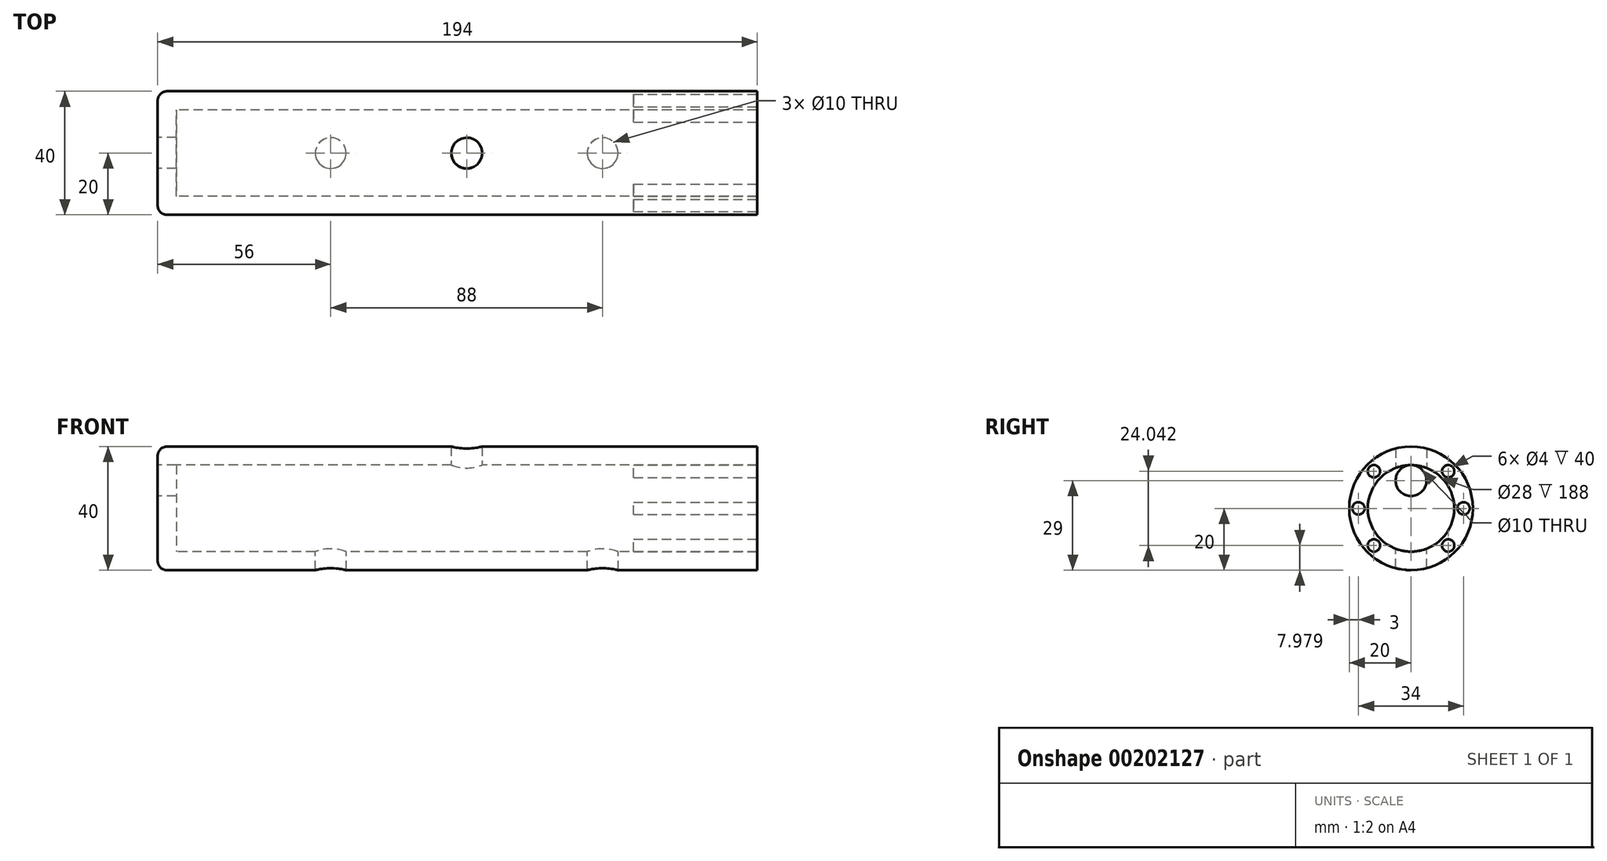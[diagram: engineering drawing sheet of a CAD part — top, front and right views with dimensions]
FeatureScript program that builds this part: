
annotation { "Feature Type Name" : "Feature", "Feature Type Description" : "" }
export const myFeature = defineFeature(function(context is Context, id is Id, definition is map)
    precondition{}
    {
        {
            var Q0;
            Q0=qCreatedBy(makeId("Right.planeOp"),FACE);
            var sketch = newSketch(context, id + "F0", { "sketchPlane" : qUnion([Q0])});
            skCircle(sketch, "E0", {"center": v(0, 0) * mm, "radius": 20 * mm});
            skSolve(sketch);
        }
        {
            var Q0;
            Q0=makeQuery(id+"F0.imprint","IMPRINT",FACE,{"disambiguationData":[TD([[makeQuery(id+"F0.imprint","IMPRINT",EDGE,{"derivedFrom":sQuery(id+"F0.wireOp",EDGE,"E0")}),1.0]])]});
            extrude(context, id + "F1", {"entities" : qUnion([Q0]), "endBound" : BoundingType.SYMMETRIC, "depth" : 194 * mm});
        }
        {
            var Q0;
            Q0=makeQuery(id+"F1.opExtrude","CAP_FACE",FACE,{"disambiguationData":[OSD([sQuery(id+"F0.wireOp",EDGE,"E0")])],"isStart":false});
            shell(context, id + "F2", {"entities" : qUnion([Q0]), "thickness" : 6 * mm});
        }
        {
            var Q0;
            Q0=makeQuery(id+"F1.opExtrude","CAP_FACE",FACE,{"disambiguationData":[OSD([sQuery(id+"F0.wireOp",EDGE,"E0")])],"isStart":false});
            var sketch = newSketch(context, id + "F3", { "sketchPlane" : qUnion([Q0])});
            skCircle(sketch, "E1.2.0", {"center": v(17, 0) * mm, "radius": 2 * mm});
            skPoint(sketch, "E1.center", {"position": v(0, 0) * mm});
            skCircle(sketch, "E2.1.0", {"center": v(12.02, -12.02) * mm, "radius": 2 * mm});
            skCircle(sketch, "E2.3.0", {"center": v(-12.02, -12.02) * mm, "radius": 2 * mm});
            skCircle(sketch, "E2.4.0", {"center": v(-17, 0) * mm, "radius": 2 * mm});
            skLineSegment(sketch, "E2.anchor1", {"start": v(0, 0) * mm, "end": v(17, 0) * mm, "construction": true});
            skLineSegment(sketch, "E2.anchor2", {"start": v(0, 0) * mm, "end": v(-17, 0) * mm, "construction": true});
            skCircle(sketch, "E3.MirrorC", {"center": v(12.02, 12.02) * mm, "radius": 2 * mm});
            skCircle(sketch, "E4.MirrorC", {"center": v(-12.02, 12.02) * mm, "radius": 2 * mm});
            skSolve(sketch);
        }
        {
            var Q0;
            Q0 = qSketchRegion(id + "F3", true);
            extrude(context, id + "F4", {"entities" : qUnion([Q0]), "operationType" : NewBodyOperationType.REMOVE, "oppositeDirection" : true, "depth" : 40 * mm});
        }
        {
            var Q0;
            Q0=makeQuery(id+"F1.opExtrude","CAP_EDGE",EDGE,{"disambiguationData":[OSD([sQuery(id+"F0.wireOp",EDGE,"E0")])],"isStart":true});
            fillet(context, id + "F5", {"entities" : qUnion([Q0]), "radius" : 3 * mm, "tangentPropagation" : true, "allowEdgeOverflow" : false});
        }
        {
            var Q0;
            Q0=qCreatedBy(makeId("Top.planeOp"),FACE);
            var sketch = newSketch(context, id + "F6", { "sketchPlane" : qUnion([Q0])});
            skCircle(sketch, "E5", {"center": v(-41, 0) * mm, "radius": 5 * mm});
            skCircle(sketch, "E6.MirrorC", {"center": v(47, 0) * mm, "radius": 5 * mm});
            skSolve(sketch);
        }
        {
            var Q0;
            Q0 = qSketchRegion(id + "F6", true);
            extrude(context, id + "F7", {"entities" : qUnion([Q0]), "operationType" : NewBodyOperationType.REMOVE, "endBound" : BoundingType.THROUGH_ALL, "oppositeDirection" : true, "depth" : 11 * mm});
        }
        {
            var Q0;
            Q0=qCreatedBy(makeId("Top.planeOp"),FACE);
            var sketch = newSketch(context, id + "F8", { "sketchPlane" : qUnion([Q0])});
            skCircle(sketch, "E7", {"center": v(3, 0) * mm, "radius": 5 * mm});
            skSolve(sketch);
        }
        {
            var Q0;
            Q0 = qSketchRegion(id + "F8", true);
            extrude(context, id + "F9", {"entities" : qUnion([Q0]), "operationType" : NewBodyOperationType.REMOVE, "endBound" : BoundingType.THROUGH_ALL, "depth" : 25 * mm});
        }
        {
            var Q0;
            Q0=makeQuery(id+"F1.opExtrude","CAP_FACE",FACE,{"disambiguationData":[OSD([sQuery(id+"F0.wireOp",EDGE,"E0")])],"isStart":true});
            var sketch = newSketch(context, id + "F10", { "sketchPlane" : qUnion([Q0])});
            skCircle(sketch, "E8", {"center": v(0, 9) * mm, "radius": 5 * mm});
            skSolve(sketch);
        }
        {
            var Q0;
            Q0=makeQuery(id+"F10.imprint","IMPRINT",FACE,{"disambiguationData":[TD([[makeQuery(id+"F10.imprint","IMPRINT",EDGE,{"derivedFrom":sQuery(id+"F10.wireOp",EDGE,"E8")}),1.0]])]});
            extrude(context, id + "F11", {"entities" : qUnion([Q0]), "operationType" : NewBodyOperationType.REMOVE, "endBound" : BoundingType.THROUGH_ALL, "oppositeDirection" : true, "depth" : 25 * mm});
        }
    });
